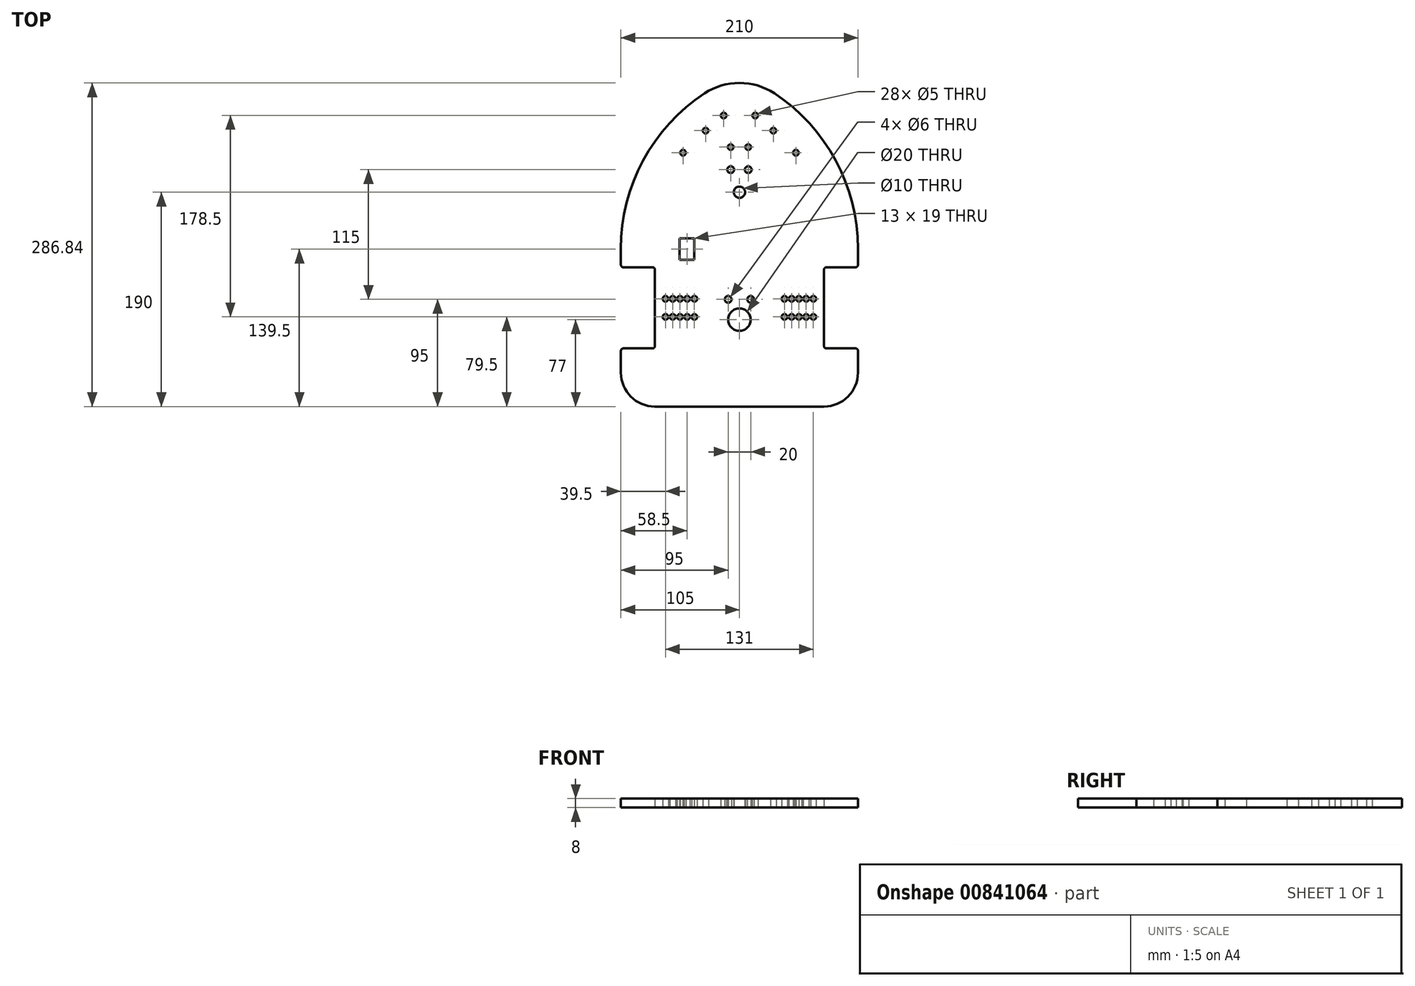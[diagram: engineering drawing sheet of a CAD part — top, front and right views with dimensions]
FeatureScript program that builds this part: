
annotation { "Feature Type Name" : "Feature", "Feature Type Description" : "" }
export const myFeature = defineFeature(function(context is Context, id is Id, definition is map)
    precondition{}
    {
        {
            var Q0;
            Q0=qCreatedBy(makeId("Top.planeOp"),FACE);
            var sketch = newSketch(context, id + "F0", { "sketchPlane" : qUnion([Q0])});
            skLineSegment(sketch, "E0.top", {"start": v(-105, -140) * mm, "end": v(105, -140) * mm});
            skLineSegment(sketch, "E0.left", {"start": v(-105, 0) * mm, "end": v(-105, -140) * mm});
            skLineSegment(sketch, "E0.right", {"start": v(105, 0) * mm, "end": v(105, -140) * mm});
            skLineSegment(sketch, "E1.bottom", {"start": v(105, -88.5) * mm, "end": v(75, -88.5) * mm});
            skLineSegment(sketch, "E1.top", {"start": v(105, -16.5) * mm, "end": v(75, -16.5) * mm});
            skLineSegment(sketch, "E1.left", {"start": v(105, -88.5) * mm, "end": v(105, -16.5) * mm});
            skLineSegment(sketch, "E1.right", {"start": v(75, -88.5) * mm, "end": v(75, -16.5) * mm});
            skLineSegment(sketch, "E2.bottom", {"start": v(-105, -88.5) * mm, "end": v(-75, -88.5) * mm});
            skLineSegment(sketch, "E2.top", {"start": v(-105, -16.5) * mm, "end": v(-75, -16.5) * mm});
            skLineSegment(sketch, "E2.left", {"start": v(-105, -88.5) * mm, "end": v(-105, -16.5) * mm});
            skLineSegment(sketch, "E2.right", {"start": v(-75, -88.5) * mm, "end": v(-75, -16.5) * mm});
            skLineSegment(sketch, "E3", {"start": v(-138.91, -52.5) * mm, "end": v(128.8, -52.5) * mm, "construction": true});
            skCircle(sketch, "E4", {"center": v(-65.5, -44.5) * mm, "radius": 2.5 * mm});
            skCircle(sketch, "E5.1.0.0", {"center": v(-59.1, -44.5) * mm, "radius": 2.5 * mm});
            skCircle(sketch, "E5.2.0.0", {"center": v(-52.7, -44.5) * mm, "radius": 2.5 * mm});
            skCircle(sketch, "E5.3.0.0", {"center": v(-46.3, -44.5) * mm, "radius": 2.5 * mm});
            skCircle(sketch, "E5.4.0.0", {"center": v(-39.9, -44.5) * mm, "radius": 2.5 * mm});
            skLineSegment(sketch, "E5.direction1", {"start": v(-65.5, -44.5) * mm, "end": v(-59.1, -44.5) * mm, "construction": true});
            skCircle(sketch, "E6", {"center": v(-65.5, -60.5) * mm, "radius": 2.5 * mm});
            skCircle(sketch, "E7.1.0.0", {"center": v(-59.1, -60.5) * mm, "radius": 2.5 * mm});
            skCircle(sketch, "E7.2.0.0", {"center": v(-52.7, -60.5) * mm, "radius": 2.5 * mm});
            skCircle(sketch, "E7.3.0.0", {"center": v(-46.3, -60.5) * mm, "radius": 2.5 * mm});
            skCircle(sketch, "E7.4.0.0", {"center": v(-39.9, -60.5) * mm, "radius": 2.5 * mm});
            skLineSegment(sketch, "E7.direction1", {"start": v(-65.5, -60.5) * mm, "end": v(-59.1, -60.5) * mm, "construction": true});
            skCircle(sketch, "E8", {"center": v(65.5, -44.5) * mm, "radius": 2.5 * mm});
            skCircle(sketch, "E9.0.1.0", {"center": v(65.5, -60.5) * mm, "radius": 2.5 * mm});
            skCircle(sketch, "E9.1.0.0", {"center": v(59.1, -44.5) * mm, "radius": 2.5 * mm});
            skCircle(sketch, "E9.1.1.0", {"center": v(59.1, -60.5) * mm, "radius": 2.5 * mm});
            skCircle(sketch, "E9.2.0.0", {"center": v(52.7, -44.5) * mm, "radius": 2.5 * mm});
            skCircle(sketch, "E9.2.1.0", {"center": v(52.7, -60.5) * mm, "radius": 2.5 * mm});
            skCircle(sketch, "E9.3.0.0", {"center": v(46.3, -44.5) * mm, "radius": 2.5 * mm});
            skCircle(sketch, "E9.3.1.0", {"center": v(46.3, -60.5) * mm, "radius": 2.5 * mm});
            skCircle(sketch, "E9.4.0.0", {"center": v(39.9, -44.5) * mm, "radius": 2.5 * mm});
            skCircle(sketch, "E9.4.1.0", {"center": v(39.9, -60.5) * mm, "radius": 2.5 * mm});
            skLineSegment(sketch, "E9.direction1", {"start": v(65.5, -44.5) * mm, "end": v(59.1, -44.5) * mm, "construction": true});
            skLineSegment(sketch, "E9.direction2", {"start": v(65.5, -44.5) * mm, "end": v(65.5, -60.5) * mm, "construction": true});
            skCircle(sketch, "E10", {"center": v(7.75, 90) * mm, "radius": 2.5 * mm});
            skCircle(sketch, "E11", {"center": v(-7.75, 90) * mm, "radius": 2.5 * mm});
            skCircle(sketch, "E12", {"center": v(-7.75, 70) * mm, "radius": 3 * mm});
            skCircle(sketch, "E13", {"center": v(7.75, 70) * mm, "radius": 3 * mm});
            skCircle(sketch, "E14", {"center": v(-10, -45) * mm, "radius": 3 * mm});
            skCircle(sketch, "E15", {"center": v(10, -45) * mm, "radius": 3 * mm});
            skArc(sketch, "E16", {"start": v(-31, 137.64) * mm, "mid": v(-85.33, 78.13) * mm, "end": v(-105, 0) * mm});
            skArc(sketch, "E17", {"start": v(105, 0) * mm, "mid": v(85.33, 78.13) * mm, "end": v(31, 137.64) * mm});
            skArc(sketch, "E18", {"start": v(31, 137.64) * mm, "mid": v(0, 146.84) * mm, "end": v(-31, 137.64) * mm});
            skCircle(sketch, "E19", {"center": v(0, -63) * mm, "radius": 10 * mm});
            skCircle(sketch, "E20", {"center": v(0, 50) * mm, "radius": 5 * mm});
            skCircle(sketch, "E21", {"center": v(-14, 118) * mm, "radius": 2.5 * mm});
            skCircle(sketch, "E22.1.0.0", {"center": v(14, 118) * mm, "radius": 2.5 * mm});
            skLineSegment(sketch, "E22.direction1", {"start": v(-14, 118) * mm, "end": v(14, 118) * mm, "construction": true});
            skCircle(sketch, "E23", {"center": v(-50, 85) * mm, "radius": 2.5 * mm});
            skCircle(sketch, "E24", {"center": v(-30, 104.6) * mm, "radius": 2.5 * mm});
            skLineSegment(sketch, "E25", {"start": v(0, -63) * mm, "end": v(0, 164.67) * mm, "construction": true});
            skCircle(sketch, "E26", {"center": v(30, 104.6) * mm, "radius": 2.5 * mm});
            skCircle(sketch, "E27", {"center": v(50, 85) * mm, "radius": 2.5 * mm});
            skLineSegment(sketch, "E28.bottom", {"start": v(-40, -10) * mm, "end": v(-53, -10) * mm});
            skLineSegment(sketch, "E28.top", {"start": v(-40, 9) * mm, "end": v(-53, 9) * mm});
            skLineSegment(sketch, "E28.left", {"start": v(-40, -10) * mm, "end": v(-40, 9) * mm});
            skLineSegment(sketch, "E28.right", {"start": v(-53, -10) * mm, "end": v(-53, 9) * mm});
            skSolve(sketch);
        }
        {
            var Q0;
            Q0=makeQuery(id+"F0.imprint","IMPRINT",FACE,{"disambiguationData":[TD([[makeQuery(id+"F0.imprint","IMPRINT",EDGE,{"derivedFrom":sQuery(id+"F0.wireOp",EDGE,"E0.top")}),1.0]])]});
            extrude(context, id + "F1", {"entities" : qUnion([Q0]), "depth" : 8 * mm, "offsetDistance" : 25 * mm});
        }
        {
            var Q0;
            Q0=makeQuery(id+"F1.opExtrude","SWEPT_EDGE",EDGE,{"disambiguationData":[OSD([sQuery(id+"F0.wireOp",EDGE,"E0.top"),sQuery(id+"F0.wireOp",EDGE,"E0.left")])]});
            var Q1;
            Q1=makeQuery(id+"F1.opExtrude","SWEPT_EDGE",EDGE,{"disambiguationData":[OSD([sQuery(id+"F0.wireOp",EDGE,"E0.top"),sQuery(id+"F0.wireOp",EDGE,"E0.right")])]});
            fillet(context, id + "F2", {"entities" : qUnion([Q0, Q1]), "radius" : 30 * mm, "tangentPropagation" : true, "allowEdgeOverflow" : false});
        }
        {
            var Q0;
            Q0=makeQuery(id+"F1.opExtrude","SWEPT_EDGE",EDGE,{"disambiguationData":[OSD([sQuery(id+"F0.wireOp",EDGE,"E2.top"),sQuery(id+"F0.wireOp",EDGE,"E2.right")])]});
            var Q1;
            Q1=makeQuery(id+"F1.opExtrude","SWEPT_EDGE",EDGE,{"disambiguationData":[OSD([sQuery(id+"F0.wireOp",EDGE,"E0.left"),sQuery(id+"F0.wireOp",EDGE,"E2.top"),sQuery(id+"F0.wireOp",EDGE,"E2.left")])]});
            var Q2;
            Q2=makeQuery(id+"F1.opExtrude","SWEPT_EDGE",EDGE,{"disambiguationData":[OSD([sQuery(id+"F0.wireOp",EDGE,"E2.bottom"),sQuery(id+"F0.wireOp",EDGE,"E2.right")])]});
            var Q3;
            Q3=makeQuery(id+"F1.opExtrude","SWEPT_EDGE",EDGE,{"disambiguationData":[OSD([sQuery(id+"F0.wireOp",EDGE,"E0.left"),sQuery(id+"F0.wireOp",EDGE,"E2.bottom"),sQuery(id+"F0.wireOp",EDGE,"E2.left")])]});
            var Q4;
            Q4=makeQuery(id+"F1.opExtrude","SWEPT_EDGE",EDGE,{"disambiguationData":[OSD([sQuery(id+"F0.wireOp",EDGE,"E1.top"),sQuery(id+"F0.wireOp",EDGE,"E1.right")])]});
            var Q5;
            Q5=makeQuery(id+"F1.opExtrude","SWEPT_EDGE",EDGE,{"disambiguationData":[OSD([sQuery(id+"F0.wireOp",EDGE,"E0.right"),sQuery(id+"F0.wireOp",EDGE,"E1.top"),sQuery(id+"F0.wireOp",EDGE,"E1.left")])]});
            var Q6;
            Q6=makeQuery(id+"F1.opExtrude","SWEPT_EDGE",EDGE,{"disambiguationData":[OSD([sQuery(id+"F0.wireOp",EDGE,"E1.bottom"),sQuery(id+"F0.wireOp",EDGE,"E1.right")])]});
            var Q7;
            Q7=makeQuery(id+"F1.opExtrude","SWEPT_EDGE",EDGE,{"disambiguationData":[OSD([sQuery(id+"F0.wireOp",EDGE,"E0.right"),sQuery(id+"F0.wireOp",EDGE,"E1.bottom"),sQuery(id+"F0.wireOp",EDGE,"E1.left")])]});
            fillet(context, id + "F3", {"entities" : qUnion([Q0, Q1, Q2, Q3, Q4, Q5, Q6, Q7]), "radius" : 2 * mm, "tangentPropagation" : true, "allowEdgeOverflow" : false});
        }
    });
